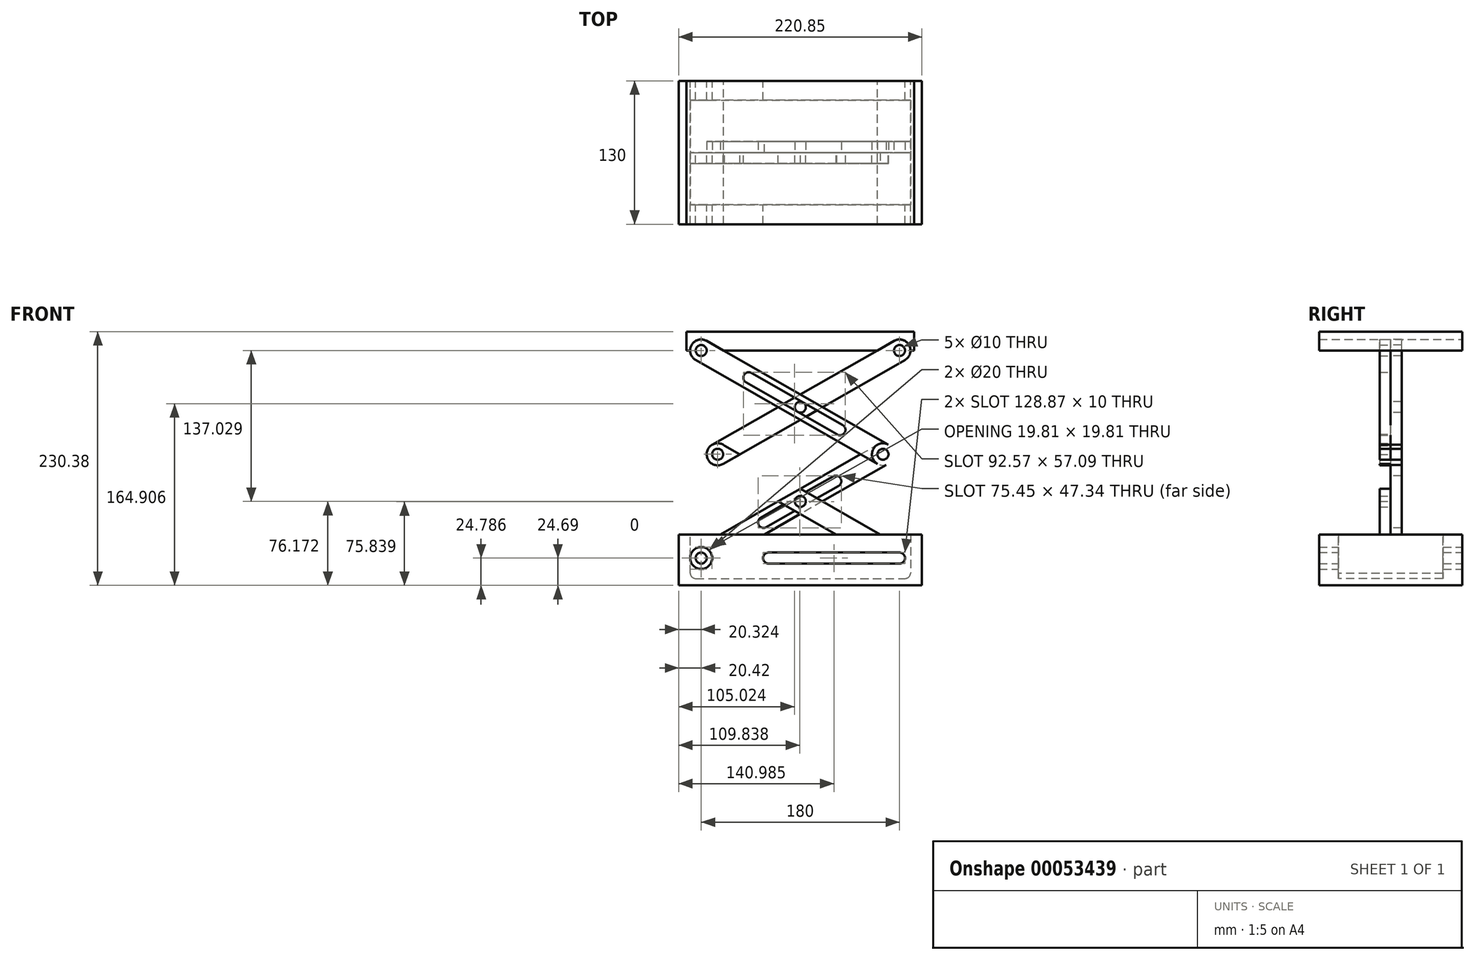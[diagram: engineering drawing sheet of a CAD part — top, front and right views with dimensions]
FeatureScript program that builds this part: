
annotation { "Feature Type Name" : "Feature", "Feature Type Description" : "" }
export const myFeature = defineFeature(function(context is Context, id is Id, definition is map)
    precondition{}
    {
        {
            var Q0;
            Q0=qCreatedBy(makeId("Front.planeOp"),FACE);
            var sketch = newSketch(context, id + "F0", { "sketchPlane" : qUnion([Q0])});
            skLineSegment(sketch, "E0", {"start": v(-81.96, 130.23) * mm, "end": v(83.04, 224.44) * mm, "construction": true});
            skLineSegment(sketch, "E1.bottom", {"start": v(96.47, 241.62) * mm, "end": v(-110.39, 241.62) * mm});
            skLineSegment(sketch, "E1.top", {"start": v(96.47, 224.44) * mm, "end": v(-110.39, 224.44) * mm});
            skLineSegment(sketch, "E1.left", {"start": v(96.47, 241.62) * mm, "end": v(96.47, 224.44) * mm});
            skLineSegment(sketch, "E1.right", {"start": v(-110.39, 241.62) * mm, "end": v(-110.39, 224.44) * mm});
            skCircle(sketch, "E2", {"center": v(83.04, 36.03) * mm, "radius": 5 * mm});
            skCircle(sketch, "E3", {"center": v(-81.96, 130.23) * mm, "radius": 5 * mm});
            skCircle(sketch, "E4", {"center": v(83.04, 224.44) * mm, "radius": 5 * mm});
            skLineSegment(sketch, "E5", {"start": v(-6.96, 224.44) * mm, "end": v(-6.96, -118.03) * mm, "construction": true});
            skCircle(sketch, "E6.MirrorC", {"center": v(-96.96, 224.44) * mm, "radius": 5 * mm});
            skCircle(sketch, "E7.MirrorC", {"center": v(-96.96, 36.03) * mm, "radius": 5 * mm});
            skLineSegment(sketch, "E8.MirrorCS", {"start": v(68.04, 130.23) * mm, "end": v(-96.96, 224.44) * mm, "construction": true});
            skLineSegment(sketch, "E9.MirrorCS", {"start": v(-96.96, 36.03) * mm, "end": v(68.04, 130.23) * mm, "construction": true});
            skCircle(sketch, "E10.MirrorC", {"center": v(68.04, 130.23) * mm, "radius": 5 * mm});
            skLineSegment(sketch, "E11.top", {"start": v(-6.96, 11.24) * mm, "end": v(103.47, 11.24) * mm});
            skLineSegment(sketch, "E11.right", {"start": v(103.47, 57.44) * mm, "end": v(103.47, 11.24) * mm});
            skLineSegment(sketch, "E12", {"start": v(-81.96, 130.23) * mm, "end": v(83.04, 36.03) * mm, "construction": true});
            skCircle(sketch, "E13", {"center": v(83.04, 36.03) * mm, "radius": 10 * mm});
            skCircle(sketch, "E14", {"center": v(-96.96, 36.03) * mm, "radius": 10 * mm});
            skCircle(sketch, "E15", {"center": v(68.04, 130.23) * mm, "radius": 10 * mm});
            skCircle(sketch, "E16", {"center": v(-81.96, 130.23) * mm, "radius": 10 * mm});
            skCircle(sketch, "E17", {"center": v(83.04, 224.44) * mm, "radius": 10 * mm});
            skCircle(sketch, "E18", {"center": v(-96.96, 224.44) * mm, "radius": 10 * mm});
            skLineSegment(sketch, "E19", {"start": v(-102.57, 44.3) * mm, "end": v(63.08, 138.92) * mm});
            skLineSegment(sketch, "E20", {"start": v(74.89, 122.95) * mm, "end": v(-91.99, 27.35) * mm});
            skLineSegment(sketch, "E21", {"start": v(77.54, 27.67) * mm, "end": v(-86.92, 121.55) * mm});
            skLineSegment(sketch, "E22", {"start": v(-75.8, 138.12) * mm, "end": v(88, 44.71) * mm});
            skLineSegment(sketch, "E23", {"start": v(88, 215.76) * mm, "end": v(-77, 121.55) * mm});
            skLineSegment(sketch, "E24", {"start": v(-86.92, 138.92) * mm, "end": v(78.08, 233.12) * mm});
            skLineSegment(sketch, "E25", {"start": v(73, 138.92) * mm, "end": v(-92, 233.12) * mm});
            skLineSegment(sketch, "E26", {"start": v(-101.92, 215.76) * mm, "end": v(63.08, 121.55) * mm});
            skArc(sketch, "E27", {"start": v(27.7, 101.45) * mm, "mid": v(29.57, 108.27) * mm, "end": v(22.75, 110.13) * mm});
            skArc(sketch, "E28", {"start": v(-42.79, 72.71) * mm, "mid": v(-44.65, 65.9) * mm, "end": v(-37.83, 64.03) * mm});
            skLineSegment(sketch, "E29", {"start": v(-42.79, 72.71) * mm, "end": v(22.75, 110.13) * mm});
            skLineSegment(sketch, "E30", {"start": v(27.7, 101.45) * mm, "end": v(-37.83, 64.03) * mm});
            skCircle(sketch, "E31", {"center": v(-6.96, 87.41) * mm, "radius": 5 * mm});
            skArc(sketch, "E32", {"start": v(-51.2, 204.07) * mm, "mid": v(-58.02, 202.2) * mm, "end": v(-56.16, 195.39) * mm});
            skArc(sketch, "E33", {"start": v(26.03, 148.5) * mm, "mid": v(33.19, 149.8) * mm, "end": v(31.48, 156.87) * mm});
            skLineSegment(sketch, "E34", {"start": v(-51.2, 204.07) * mm, "end": v(31.48, 156.87) * mm});
            skLineSegment(sketch, "E35", {"start": v(27.05, 147.92) * mm, "end": v(-56.16, 195.39) * mm});
            skCircle(sketch, "E36", {"center": v(-6.96, 173.05) * mm, "radius": 4.98 * mm});
            skLineSegment(sketch, "E37.MirrorCS", {"start": v(-6.96, 11.24) * mm, "end": v(-117.38, 11.24) * mm});
            skLineSegment(sketch, "E38.MirrorCS", {"start": v(-117.38, 57.44) * mm, "end": v(-117.38, 11.24) * mm});
            skLineSegment(sketch, "E39", {"start": v(-117.38, 57.44) * mm, "end": v(103.47, 57.44) * mm});
            skLineSegment(sketch, "E40", {"start": v(83.04, 36.03) * mm, "end": v(-35.83, 36.03) * mm, "construction": true});
            skCircle(sketch, "E41", {"center": v(-35.83, 36.03) * mm, "radius": 5 * mm});
            skLineSegment(sketch, "E42", {"start": v(83.04, 41.03) * mm, "end": v(-35.83, 41.03) * mm});
            skLineSegment(sketch, "E43", {"start": v(-35.83, 31.03) * mm, "end": v(83.04, 31.03) * mm});
            skSolve(sketch);
        }
        {
            var Q0;
            Q0=makeQuery(id+"F0.imprint","IMPRINT",FACE,{"disambiguationData":[TD([[makeQuery(id+"F0.imprint","IMPRINT",EDGE,{"derivedFrom":sQuery(id+"F0.wireOp",EDGE,"E11.top")}),1.0]])]});
            var Q1;
            {var subQ2=sQuery(id+"F0.wireOp",EDGE,"E42");var subQ7=sQuery(id+"F0.wireOp",EDGE,"E2");var subQ9=makeQuery(id+"F0.imprint","INTERSECT",VERTEX,{"derivedFrom":[subQ7,subQ2]});Q1=makeQuery(id+"F0.imprint","IMPRINT",FACE,{"disambiguationData":[TD([[makeQuery(id+"F0.imprint","IMPRINT",EDGE,{"disambiguationData":[TD([[subQ9,1.0]])],"derivedFrom":subQ7}),-1.0]])]});}
            var Q2;
            {var subQ0=sQuery(id+"F0.wireOp",EDGE,"E22");var subQ1=sQuery(id+"F0.wireOp",EDGE,"E13");var subQ2=makeQuery(id+"F0.imprint","INTERSECT",VERTEX,{"derivedFrom":[subQ1,subQ0]});Q2=makeQuery(id+"F0.imprint","IMPRINT",FACE,{"disambiguationData":[TD([[makeQuery(id+"F0.imprint","IMPRINT",EDGE,{"disambiguationData":[TD([[subQ2,-1.0]])],"derivedFrom":subQ1}),-1.0]])]});}
            var Q3;
            {var subQ0=sQuery(id+"F0.wireOp",EDGE,"E20");var subQ1=sQuery(id+"F0.wireOp",EDGE,"E14");var subQ2=makeQuery(id+"F0.imprint","INTERSECT",VERTEX,{"derivedFrom":[subQ1,subQ0]});Q3=makeQuery(id+"F0.imprint","IMPRINT",FACE,{"disambiguationData":[TD([[makeQuery(id+"F0.imprint","IMPRINT",EDGE,{"disambiguationData":[TD([[subQ2,-1.0]])],"derivedFrom":subQ1}),-1.0]])]});}
            var Q4;
            Q4=makeQuery(id+"F0.imprint","IMPRINT",FACE,{"disambiguationData":[TD([[makeQuery(id+"F0.imprint","IMPRINT",EDGE,{"derivedFrom":sQuery(id+"F0.wireOp",EDGE,"E7.MirrorC")}),1.0]])]});
            var Q5;
            {var subQ0=sQuery(id+"F0.wireOp",EDGE,"E21");var subQ1=sQuery(id+"F0.wireOp",EDGE,"E13");var subQ2=makeQuery(id+"F0.imprint","INTERSECT",VERTEX,{"derivedFrom":[subQ1,subQ0]});Q5=makeQuery(id+"F0.imprint","IMPRINT",FACE,{"disambiguationData":[TD([[makeQuery(id+"F0.imprint","IMPRINT",EDGE,{"disambiguationData":[TD([[subQ2,1.0]])],"derivedFrom":subQ1}),-1.0]])]});}
            extrude(context, id + "F1", {"entities" : qUnion([Q0, Q1, Q2, Q3, Q4, Q5]), "endBound" : BoundingType.SYMMETRIC, "depth" : 130 * mm});
        }
        {
            var Q0;
            Q0=makeQuery(id+"F0.imprint","IMPRINT",FACE,{"disambiguationData":[TD([[makeQuery(id+"F0.imprint","IMPRINT",EDGE,{"derivedFrom":sQuery(id+"F0.wireOp",EDGE,"E1.bottom")}),1.0]])]});
            extrude(context, id + "F2", {"entities" : qUnion([Q0]), "endBound" : BoundingType.SYMMETRIC, "depth" : 130 * mm});
        }
        {
            var Q0;
            {var subQ3=sQuery(id+"F0.wireOp",EDGE,"E25");var subQ5=sQuery(id+"F0.wireOp",EDGE,"E1.top");var subQ6=makeQuery(id+"F0.imprint","INTERSECT",VERTEX,{"derivedFrom":[subQ5,subQ3]});Q0=makeQuery(id+"F0.imprint","IMPRINT",FACE,{"disambiguationData":[TD([[makeQuery(id+"F0.imprint","IMPRINT",EDGE,{"disambiguationData":[TD([[subQ6,-1.0]])],"derivedFrom":subQ5}),1.0]])]});}
            var Q1;
            {var subQ0=sQuery(id+"F0.wireOp",EDGE,"E25");var subQ1=sQuery(id+"F0.wireOp",EDGE,"E1.top");var subQ2=makeQuery(id+"F0.imprint","INTERSECT",VERTEX,{"derivedFrom":[subQ1,subQ0]});Q1=makeQuery(id+"F0.imprint","IMPRINT",FACE,{"disambiguationData":[TD([[makeQuery(id+"F0.imprint","IMPRINT",EDGE,{"disambiguationData":[TD([[subQ2,-1.0]])],"derivedFrom":subQ1}),-1.0]])]});}
            var Q2;
            {var subQ0=sQuery(id+"F0.wireOp",EDGE,"E18");var subQ1=sQuery(id+"F0.wireOp",EDGE,"E1.top");var subQ2=makeQuery(id+"F0.imprint","INTERSECT",VERTEX,{"disambiguationData":[OD(1.0)],"derivedFrom":[subQ1,subQ0]});Q2=makeQuery(id+"F0.imprint","IMPRINT",FACE,{"disambiguationData":[TD([[makeQuery(id+"F0.imprint","IMPRINT",EDGE,{"disambiguationData":[TD([[subQ2,-1.0]])],"derivedFrom":subQ1}),-1.0]])]});}
            var Q3;
            {var subQ1=sQuery(id+"F0.wireOp",EDGE,"E18");var subQ3=sQuery(id+"F0.wireOp",EDGE,"E1.top");var subQ8=makeQuery(id+"F0.imprint","INTERSECT",VERTEX,{"disambiguationData":[OD(1.0)],"derivedFrom":[subQ3,subQ1]});Q3=makeQuery(id+"F0.imprint","IMPRINT",FACE,{"disambiguationData":[TD([[makeQuery(id+"F0.imprint","IMPRINT",EDGE,{"disambiguationData":[TD([[subQ8,-1.0]])],"derivedFrom":subQ3}),1.0]])]});}
            var Q4;
            {var subQ0=sQuery(id+"F0.wireOp",EDGE,"E25");var subQ1=sQuery(id+"F0.wireOp",EDGE,"E23");var subQ2=makeQuery(id+"F0.imprint","INTERSECT",VERTEX,{"derivedFrom":[subQ1,subQ0]});Q4=makeQuery(id+"F0.imprint","IMPRINT",FACE,{"disambiguationData":[TD([[makeQuery(id+"F0.imprint","IMPRINT",EDGE,{"disambiguationData":[TD([[subQ2,-1.0]])],"derivedFrom":subQ1}),-1.0]])]});}
            var Q5;
            {var subQ5=sQuery(id+"F0.wireOp",EDGE,"E19");var subQ6=sQuery(id+"F0.wireOp",EDGE,"E15");var subQ7=makeQuery(id+"F0.imprint","INTERSECT",VERTEX,{"derivedFrom":[subQ6,subQ5]});Q5=makeQuery(id+"F0.imprint","IMPRINT",FACE,{"disambiguationData":[TD([[makeQuery(id+"F0.imprint","IMPRINT",EDGE,{"disambiguationData":[TD([[subQ7,1.0]])],"derivedFrom":subQ6}),-1.0]])]});}
            var Q6;
            {var subQ0=sQuery(id+"F0.wireOp",EDGE,"E19");var subQ1=sQuery(id+"F0.wireOp",EDGE,"E15");var subQ2=makeQuery(id+"F0.imprint","INTERSECT",VERTEX,{"derivedFrom":[subQ1,subQ0]});Q6=makeQuery(id+"F0.imprint","IMPRINT",FACE,{"disambiguationData":[TD([[makeQuery(id+"F0.imprint","IMPRINT",EDGE,{"disambiguationData":[TD([[subQ2,-1.0]])],"derivedFrom":subQ1}),-1.0]])]});}
            var Q7;
            Q7=makeQuery(id+"F0.imprint","IMPRINT",FACE,{"disambiguationData":[TD([[makeQuery(id+"F0.imprint","IMPRINT",EDGE,{"derivedFrom":sQuery(id+"F0.wireOp",EDGE,"E10.MirrorC")}),1.0]])]});
            var Q8;
            {var subQ1=sQuery(id+"F0.wireOp",EDGE,"E16");var subQ9=makeQuery(id+"F0.imprint","IMPRINT",VERTEX,{"derivedFrom":subQ1});Q8=makeQuery(id+"F0.imprint","IMPRINT",FACE,{"disambiguationData":[TD([[makeQuery(id+"F0.imprint","IMPRINT",EDGE,{"disambiguationData":[TD([[subQ9,1.0]])],"derivedFrom":subQ1}),-1.0]])]});}
            var Q9;
            {var subQ0=sQuery(id+"F0.wireOp",EDGE,"E22");var subQ1=sQuery(id+"F0.wireOp",EDGE,"E16");var subQ2=makeQuery(id+"F0.imprint","INTERSECT",VERTEX,{"derivedFrom":[subQ1,subQ0]});Q9=makeQuery(id+"F0.imprint","IMPRINT",FACE,{"disambiguationData":[TD([[makeQuery(id+"F0.imprint","IMPRINT",EDGE,{"disambiguationData":[TD([[subQ2,1.0]])],"derivedFrom":subQ1}),-1.0]])]});}
            var Q10;
            Q10=makeQuery(id+"F0.imprint","IMPRINT",FACE,{"disambiguationData":[TD([[makeQuery(id+"F0.imprint","IMPRINT",EDGE,{"derivedFrom":sQuery(id+"F0.wireOp",EDGE,"E3")}),-1.0]])]});
            var Q11;
            {var subQ0=sQuery(id+"F0.wireOp",EDGE,"E21");var subQ1=sQuery(id+"F0.wireOp",EDGE,"E19");var subQ2=makeQuery(id+"F0.imprint","INTERSECT",VERTEX,{"derivedFrom":[subQ1,subQ0]});Q11=makeQuery(id+"F0.imprint","IMPRINT",FACE,{"disambiguationData":[TD([[makeQuery(id+"F0.imprint","IMPRINT",EDGE,{"disambiguationData":[TD([[subQ2,-1.0]])],"derivedFrom":subQ1}),-1.0]])]});}
            var Q12;
            {var subQ0=sQuery(id+"F0.wireOp",EDGE,"E21");var subQ1=sQuery(id+"F0.wireOp",EDGE,"E11.bottom");var subQ2=makeQuery(id+"F0.imprint","INTERSECT",VERTEX,{"derivedFrom":[subQ1,subQ0]});Q12=makeQuery(id+"F0.imprint","IMPRINT",FACE,{"disambiguationData":[TD([[makeQuery(id+"F0.imprint","IMPRINT",EDGE,{"disambiguationData":[TD([[subQ2,-1.0]])],"derivedFrom":subQ1}),1.0]])]});}
            var Q13;
            {var subQ2=sQuery(id+"F0.wireOp",EDGE,"E11.bottom");var subQ4=sQuery(id+"F0.wireOp",EDGE,"E2");var subQ5=makeQuery(id+"F0.imprint","INTERSECT",VERTEX,{"disambiguationData":[OD(0.0)],"derivedFrom":[subQ4,subQ2]});Q13=makeQuery(id+"F0.imprint","IMPRINT",FACE,{"disambiguationData":[TD([[makeQuery(id+"F0.imprint","IMPRINT",EDGE,{"disambiguationData":[TD([[subQ5,1.0]])],"derivedFrom":subQ4}),-1.0]])]});}
            var Q14;
            {var subQ2=sQuery(id+"F0.wireOp",EDGE,"E11.bottom");var subQ5=sQuery(id+"F0.wireOp",EDGE,"E2");var subQ7=makeQuery(id+"F0.imprint","INTERSECT",VERTEX,{"disambiguationData":[OD(0.0)],"derivedFrom":[subQ5,subQ2]});Q14=makeQuery(id+"F0.imprint","IMPRINT",FACE,{"disambiguationData":[TD([[makeQuery(id+"F0.imprint","IMPRINT",EDGE,{"disambiguationData":[TD([[subQ7,-1.0]])],"derivedFrom":subQ5}),-1.0]])]});}
            var Q15;
            {var subQ0=sQuery(id+"F0.wireOp",EDGE,"E21");var subQ1=sQuery(id+"F0.wireOp",EDGE,"E11.bottom");var subQ2=makeQuery(id+"F0.imprint","INTERSECT",VERTEX,{"derivedFrom":[subQ1,subQ0]});Q15=makeQuery(id+"F0.imprint","IMPRINT",FACE,{"disambiguationData":[TD([[makeQuery(id+"F0.imprint","IMPRINT",EDGE,{"disambiguationData":[TD([[subQ2,-1.0]])],"derivedFrom":subQ1}),-1.0]])]});}
            var Q16;
            {var subQ0=sQuery(id+"F0.wireOp",EDGE,"E29");var subQ1=sQuery(id+"F0.wireOp",EDGE,"E22");var subQ2=makeQuery(id+"F0.imprint","INTERSECT",VERTEX,{"derivedFrom":[subQ1,subQ0]});Q16=makeQuery(id+"F0.imprint","IMPRINT",FACE,{"disambiguationData":[TD([[makeQuery(id+"F0.imprint","IMPRINT",EDGE,{"disambiguationData":[TD([[subQ2,-1.0]])],"derivedFrom":subQ1}),-1.0]])]});}
            var Q17;
            {var subQ0=sQuery(id+"F0.wireOp",EDGE,"E35");var subQ2=sQuery(id+"F0.wireOp",EDGE,"E23");var subQ3=makeQuery(id+"F0.imprint","INTERSECT",VERTEX,{"derivedFrom":[subQ2,subQ0]});Q17=makeQuery(id+"F0.imprint","IMPRINT",FACE,{"disambiguationData":[TD([[makeQuery(id+"F0.imprint","IMPRINT",EDGE,{"disambiguationData":[TD([[subQ3,-1.0]])],"derivedFrom":subQ2}),-1.0]])]});}
            var Q18;
            {var subQ0=sQuery(id+"F0.wireOp",EDGE,"E30");var subQ1=sQuery(id+"F0.wireOp",EDGE,"E21");var subQ2=makeQuery(id+"F0.imprint","INTERSECT",VERTEX,{"derivedFrom":[subQ1,subQ0]});Q18=makeQuery(id+"F0.imprint","IMPRINT",FACE,{"disambiguationData":[TD([[makeQuery(id+"F0.imprint","IMPRINT",EDGE,{"disambiguationData":[TD([[subQ2,-1.0]])],"derivedFrom":subQ1}),-1.0]])]});}
            var Q19;
            {var subQ1=sQuery(id+"F0.wireOp",EDGE,"E22");var subQ4=sQuery(id+"F0.wireOp",EDGE,"E20");var subQ5=makeQuery(id+"F0.imprint","INTERSECT",VERTEX,{"derivedFrom":[subQ4,subQ1]});Q19=makeQuery(id+"F0.imprint","IMPRINT",FACE,{"disambiguationData":[TD([[makeQuery(id+"F0.imprint","IMPRINT",EDGE,{"disambiguationData":[TD([[subQ5,-1.0]])],"derivedFrom":subQ4}),-1.0]])]});}
            var Q20;
            {var subQ0=sQuery(id+"F0.wireOp",EDGE,"E22");var subQ1=sQuery(id+"F0.wireOp",EDGE,"E20");var subQ2=makeQuery(id+"F0.imprint","INTERSECT",VERTEX,{"derivedFrom":[subQ1,subQ0]});Q20=makeQuery(id+"F0.imprint","IMPRINT",FACE,{"disambiguationData":[TD([[makeQuery(id+"F0.imprint","IMPRINT",EDGE,{"disambiguationData":[TD([[subQ2,-1.0]])],"derivedFrom":subQ1}),1.0]])]});}
            var Q21;
            {var subQ0=sQuery(id+"F0.wireOp",EDGE,"E22");var subQ1=sQuery(id+"F0.wireOp",EDGE,"E13");var subQ2=makeQuery(id+"F0.imprint","INTERSECT",VERTEX,{"derivedFrom":[subQ1,subQ0]});Q21=makeQuery(id+"F0.imprint","IMPRINT",FACE,{"disambiguationData":[TD([[makeQuery(id+"F0.imprint","IMPRINT",EDGE,{"disambiguationData":[TD([[subQ2,-1.0]])],"derivedFrom":subQ1}),-1.0]])]});}
            var Q22;
            {var subQ0=sQuery(id+"F0.wireOp",EDGE,"E42");var subQ1=sQuery(id+"F0.wireOp",EDGE,"E13");var subQ2=makeQuery(id+"F0.imprint","INTERSECT",VERTEX,{"derivedFrom":[subQ1,subQ0]});Q22=makeQuery(id+"F0.imprint","IMPRINT",FACE,{"disambiguationData":[TD([[makeQuery(id+"F0.imprint","IMPRINT",EDGE,{"disambiguationData":[TD([[subQ2,-1.0]])],"derivedFrom":subQ1}),-1.0]])]});}
            var Q23;
            {var subQ2=sQuery(id+"F0.wireOp",EDGE,"E42");var subQ7=sQuery(id+"F0.wireOp",EDGE,"E2");var subQ9=makeQuery(id+"F0.imprint","INTERSECT",VERTEX,{"derivedFrom":[subQ7,subQ2]});Q23=makeQuery(id+"F0.imprint","IMPRINT",FACE,{"disambiguationData":[TD([[makeQuery(id+"F0.imprint","IMPRINT",EDGE,{"disambiguationData":[TD([[subQ9,1.0]])],"derivedFrom":subQ7}),-1.0]])]});}
            var Q24;
            {var subQ0=sQuery(id+"F0.wireOp",EDGE,"E21");var subQ1=sQuery(id+"F0.wireOp",EDGE,"E13");var subQ2=makeQuery(id+"F0.imprint","INTERSECT",VERTEX,{"derivedFrom":[subQ1,subQ0]});Q24=makeQuery(id+"F0.imprint","IMPRINT",FACE,{"disambiguationData":[TD([[makeQuery(id+"F0.imprint","IMPRINT",EDGE,{"disambiguationData":[TD([[subQ2,1.0]])],"derivedFrom":subQ1}),-1.0]])]});}
            extrude(context, id + "F3", {"entities" : qUnion([Q0, Q1, Q2, Q3, Q4, Q5, Q6, Q7, Q8, Q9, Q10, Q11, Q12, Q13, Q14, Q15, Q16, Q17, Q18, Q19, Q20, Q21, Q22, Q23, Q24]), "depth" : 10 * mm});
        }
        {
            var Q0;
            {var subQ1=sQuery(id+"F0.wireOp",EDGE,"E17");var subQ5=sQuery(id+"F0.wireOp",EDGE,"E1.top");var subQ6=makeQuery(id+"F0.imprint","INTERSECT",VERTEX,{"disambiguationData":[OD(1.0)],"derivedFrom":[subQ5,subQ1]});Q0=makeQuery(id+"F0.imprint","IMPRINT",FACE,{"disambiguationData":[TD([[makeQuery(id+"F0.imprint","IMPRINT",EDGE,{"disambiguationData":[TD([[subQ6,-1.0]])],"derivedFrom":subQ5}),1.0]])]});}
            var Q1;
            {var subQ1=sQuery(id+"F0.wireOp",EDGE,"E17");var subQ3=sQuery(id+"F0.wireOp",EDGE,"E1.top");var subQ9=makeQuery(id+"F0.imprint","INTERSECT",VERTEX,{"disambiguationData":[OD(0.0)],"derivedFrom":[subQ3,subQ1]});Q1=makeQuery(id+"F0.imprint","IMPRINT",FACE,{"disambiguationData":[TD([[makeQuery(id+"F0.imprint","IMPRINT",EDGE,{"disambiguationData":[TD([[subQ9,-1.0]])],"derivedFrom":subQ3}),1.0]])]});}
            var Q2;
            {var subQ0=sQuery(id+"F0.wireOp",EDGE,"E17");var subQ2=sQuery(id+"F0.wireOp",EDGE,"E1.top");var subQ3=makeQuery(id+"F0.imprint","INTERSECT",VERTEX,{"disambiguationData":[OD(0.0)],"derivedFrom":[subQ2,subQ0]});Q2=makeQuery(id+"F0.imprint","IMPRINT",FACE,{"disambiguationData":[TD([[makeQuery(id+"F0.imprint","IMPRINT",EDGE,{"disambiguationData":[TD([[subQ3,-1.0]])],"derivedFrom":subQ2}),-1.0]])]});}
            var Q3;
            {var subQ0=sQuery(id+"F0.wireOp",EDGE,"E17");var subQ1=sQuery(id+"F0.wireOp",EDGE,"E1.top");var subQ2=makeQuery(id+"F0.imprint","INTERSECT",VERTEX,{"disambiguationData":[OD(1.0)],"derivedFrom":[subQ1,subQ0]});Q3=makeQuery(id+"F0.imprint","IMPRINT",FACE,{"disambiguationData":[TD([[makeQuery(id+"F0.imprint","IMPRINT",EDGE,{"disambiguationData":[TD([[subQ2,-1.0]])],"derivedFrom":subQ1}),-1.0]])]});}
            var Q4;
            {var subQ0=sQuery(id+"F0.wireOp",EDGE,"E25");var subQ1=sQuery(id+"F0.wireOp",EDGE,"E23");var subQ2=makeQuery(id+"F0.imprint","INTERSECT",VERTEX,{"derivedFrom":[subQ1,subQ0]});Q4=makeQuery(id+"F0.imprint","IMPRINT",FACE,{"disambiguationData":[TD([[makeQuery(id+"F0.imprint","IMPRINT",EDGE,{"disambiguationData":[TD([[subQ2,-1.0]])],"derivedFrom":subQ1}),-1.0]])]});}
            var Q5;
            {var subQ1=sQuery(id+"F0.wireOp",EDGE,"E16");var subQ6=sQuery(id+"F0.wireOp",EDGE,"E22");var subQ9=makeQuery(id+"F0.imprint","INTERSECT",VERTEX,{"derivedFrom":[subQ1,subQ6]});Q5=makeQuery(id+"F0.imprint","IMPRINT",FACE,{"disambiguationData":[TD([[makeQuery(id+"F0.imprint","IMPRINT",EDGE,{"disambiguationData":[TD([[subQ9,-1.0]])],"derivedFrom":subQ1}),-1.0]])]});}
            var Q6;
            {var subQ0=sQuery(id+"F0.wireOp",EDGE,"E22");var subQ1=sQuery(id+"F0.wireOp",EDGE,"E16");var subQ2=makeQuery(id+"F0.imprint","INTERSECT",VERTEX,{"derivedFrom":[subQ1,subQ0]});Q6=makeQuery(id+"F0.imprint","IMPRINT",FACE,{"disambiguationData":[TD([[makeQuery(id+"F0.imprint","IMPRINT",EDGE,{"disambiguationData":[TD([[subQ2,1.0]])],"derivedFrom":subQ1}),-1.0]])]});}
            var Q7;
            Q7=makeQuery(id+"F0.imprint","IMPRINT",FACE,{"disambiguationData":[TD([[makeQuery(id+"F0.imprint","IMPRINT",EDGE,{"derivedFrom":sQuery(id+"F0.wireOp",EDGE,"E3")}),-1.0]])]});
            var Q8;
            {var subQ5=sQuery(id+"F0.wireOp",EDGE,"E15");var subQ7=sQuery(id+"F0.wireOp",EDGE,"E26");var subQ9=makeQuery(id+"F0.imprint","INTERSECT",VERTEX,{"derivedFrom":[subQ5,subQ7]});Q8=makeQuery(id+"F0.imprint","IMPRINT",FACE,{"disambiguationData":[TD([[makeQuery(id+"F0.imprint","IMPRINT",EDGE,{"disambiguationData":[TD([[subQ9,-1.0]])],"derivedFrom":subQ5}),-1.0]])]});}
            var Q9;
            Q9=makeQuery(id+"F0.imprint","IMPRINT",FACE,{"disambiguationData":[TD([[makeQuery(id+"F0.imprint","IMPRINT",EDGE,{"derivedFrom":sQuery(id+"F0.wireOp",EDGE,"E10.MirrorC")}),1.0]])]});
            var Q10;
            {var subQ0=sQuery(id+"F0.wireOp",EDGE,"E19");var subQ1=sQuery(id+"F0.wireOp",EDGE,"E15");var subQ2=makeQuery(id+"F0.imprint","INTERSECT",VERTEX,{"derivedFrom":[subQ1,subQ0]});Q10=makeQuery(id+"F0.imprint","IMPRINT",FACE,{"disambiguationData":[TD([[makeQuery(id+"F0.imprint","IMPRINT",EDGE,{"disambiguationData":[TD([[subQ2,-1.0]])],"derivedFrom":subQ1}),-1.0]])]});}
            var Q11;
            {var subQ0=sQuery(id+"F0.wireOp",EDGE,"E21");var subQ1=sQuery(id+"F0.wireOp",EDGE,"E19");var subQ2=makeQuery(id+"F0.imprint","INTERSECT",VERTEX,{"derivedFrom":[subQ1,subQ0]});Q11=makeQuery(id+"F0.imprint","IMPRINT",FACE,{"disambiguationData":[TD([[makeQuery(id+"F0.imprint","IMPRINT",EDGE,{"disambiguationData":[TD([[subQ2,-1.0]])],"derivedFrom":subQ1}),-1.0]])]});}
            var Q12;
            {var subQ1=sQuery(id+"F0.wireOp",EDGE,"E11.bottom");var subQ6=sQuery(id+"F0.wireOp",EDGE,"E14");var subQ9=makeQuery(id+"F0.imprint","INTERSECT",VERTEX,{"disambiguationData":[OD(1.0)],"derivedFrom":[subQ1,subQ6]});Q12=makeQuery(id+"F0.imprint","IMPRINT",FACE,{"disambiguationData":[TD([[makeQuery(id+"F0.imprint","IMPRINT",EDGE,{"disambiguationData":[TD([[subQ9,-1.0]])],"derivedFrom":subQ1}),1.0]])]});}
            var Q13;
            {var subQ3=sQuery(id+"F0.wireOp",EDGE,"E11.bottom");var subQ5=sQuery(id+"F0.wireOp",EDGE,"E7.MirrorC");var subQ8=makeQuery(id+"F0.imprint","INTERSECT",VERTEX,{"disambiguationData":[OD(0.0)],"derivedFrom":[subQ5,subQ3]});Q13=makeQuery(id+"F0.imprint","IMPRINT",FACE,{"disambiguationData":[TD([[makeQuery(id+"F0.imprint","IMPRINT",EDGE,{"disambiguationData":[TD([[subQ8,-1.0]])],"derivedFrom":subQ5}),1.0]])]});}
            var Q14;
            {var subQ2=sQuery(id+"F0.wireOp",EDGE,"E11.bottom");var subQ4=sQuery(id+"F0.wireOp",EDGE,"E7.MirrorC");var subQ5=makeQuery(id+"F0.imprint","INTERSECT",VERTEX,{"disambiguationData":[OD(0.0)],"derivedFrom":[subQ4,subQ2]});Q14=makeQuery(id+"F0.imprint","IMPRINT",FACE,{"disambiguationData":[TD([[makeQuery(id+"F0.imprint","IMPRINT",EDGE,{"disambiguationData":[TD([[subQ5,1.0]])],"derivedFrom":subQ4}),1.0]])]});}
            var Q15;
            {var subQ0=sQuery(id+"F0.wireOp",EDGE,"E14");var subQ1=sQuery(id+"F0.wireOp",EDGE,"E11.bottom");var subQ2=makeQuery(id+"F0.imprint","INTERSECT",VERTEX,{"disambiguationData":[OD(1.0)],"derivedFrom":[subQ1,subQ0]});Q15=makeQuery(id+"F0.imprint","IMPRINT",FACE,{"disambiguationData":[TD([[makeQuery(id+"F0.imprint","IMPRINT",EDGE,{"disambiguationData":[TD([[subQ2,-1.0]])],"derivedFrom":subQ1}),-1.0]])]});}
            var Q16;
            {var subQ0=sQuery(id+"F0.wireOp",EDGE,"E22");var subQ1=sQuery(id+"F0.wireOp",EDGE,"E20");var subQ2=makeQuery(id+"F0.imprint","INTERSECT",VERTEX,{"derivedFrom":[subQ1,subQ0]});Q16=makeQuery(id+"F0.imprint","IMPRINT",FACE,{"disambiguationData":[TD([[makeQuery(id+"F0.imprint","IMPRINT",EDGE,{"disambiguationData":[TD([[subQ2,-1.0]])],"derivedFrom":subQ1}),-1.0]])]});}
            var Q17;
            {var subQ0=sQuery(id+"F0.wireOp",EDGE,"E35");var subQ2=sQuery(id+"F0.wireOp",EDGE,"E23");var subQ3=makeQuery(id+"F0.imprint","INTERSECT",VERTEX,{"derivedFrom":[subQ2,subQ0]});Q17=makeQuery(id+"F0.imprint","IMPRINT",FACE,{"disambiguationData":[TD([[makeQuery(id+"F0.imprint","IMPRINT",EDGE,{"disambiguationData":[TD([[subQ3,-1.0]])],"derivedFrom":subQ2}),-1.0]])]});}
            var Q18;
            {var subQ0=sQuery(id+"F0.wireOp",EDGE,"E36");Q18=makeQuery(id+"F0.imprint","IMPRINT",FACE,{"disambiguationData":[TD([[makeQuery(id+"F0.imprint","IMPRINT",EDGE,{"derivedFrom":subQ0}),-1.0]])]});}
            var Q19;
            {var subQ11=sQuery(id+"F0.wireOp",EDGE,"E28");Q19=makeQuery(id+"F0.imprint","IMPRINT",FACE,{"disambiguationData":[TD([[makeQuery(id+"F0.imprint","IMPRINT",EDGE,{"derivedFrom":subQ11}),-1.0]])]});}
            var Q20;
            {var subQ0=sQuery(id+"F0.wireOp",EDGE,"E20");var subQ1=sQuery(id+"F0.wireOp",EDGE,"E14");var subQ2=makeQuery(id+"F0.imprint","INTERSECT",VERTEX,{"derivedFrom":[subQ1,subQ0]});Q20=makeQuery(id+"F0.imprint","IMPRINT",FACE,{"disambiguationData":[TD([[makeQuery(id+"F0.imprint","IMPRINT",EDGE,{"disambiguationData":[TD([[subQ2,-1.0]])],"derivedFrom":subQ1}),-1.0]])]});}
            var Q21;
            Q21=makeQuery(id+"F0.imprint","IMPRINT",FACE,{"disambiguationData":[TD([[makeQuery(id+"F0.imprint","IMPRINT",EDGE,{"derivedFrom":sQuery(id+"F0.wireOp",EDGE,"E7.MirrorC")}),1.0]])]});
            extrude(context, id + "F4", {"entities" : qUnion([Q0, Q1, Q2, Q3, Q4, Q5, Q6, Q7, Q8, Q9, Q10, Q11, Q12, Q13, Q14, Q15, Q16, Q17, Q18, Q19, Q20, Q21]), "oppositeDirection" : true, "depth" : 10 * mm});
        }
        {
            var Q0;
            Q0=qCreatedBy(makeId("Front.planeOp"),FACE);
            var sketch = newSketch(context, id + "F5", { "sketchPlane" : qUnion([Q0])});
            skLineSegment(sketch, "E44.top", {"start": v(-101.96, 17.44) * mm, "end": v(88.04, 17.44) * mm});
            skPoint(sketch, "E45.visualSharp", {"position": v(-106.96, 17.44) * mm});
            skArc(sketch, "E45.filletArc", {"start": v(-106.96, 22.24) * mm, "mid": v(-105.43, 18.84) * mm, "end": v(-101.96, 17.44) * mm});
            skLineSegment(sketch, "E46.0.0", {"start": v(93.04, 57.44) * mm, "end": v(-106.96, 57.44) * mm});
            skLineSegment(sketch, "E47", {"start": v(-6.96, 57.44) * mm, "end": v(-6.96, 11.24) * mm, "construction": true});
            skLineSegment(sketch, "E48.MirrorCS", {"start": v(93.04, 57.44) * mm, "end": v(93.04, 22.44) * mm});
            skPoint(sketch, "E49.orphan", {"position": v(93.04, 22.24) * mm});
            skPoint(sketch, "E50.visualSharp", {"position": v(93.04, 17.44) * mm});
            skArc(sketch, "E50.filletArc", {"start": v(88.04, 17.44) * mm, "mid": v(91.58, 18.9) * mm, "end": v(93.04, 22.44) * mm});
            skLineSegment(sketch, "E51", {"start": v(-106.96, 22.24) * mm, "end": v(-106.96, 57.44) * mm});
            skSolve(sketch);
        }
        {
            var Q0;
            Q0=makeQuery(id+"F5.imprint","IMPRINT",FACE,{"disambiguationData":[TD([[makeQuery(id+"F5.imprint","IMPRINT",EDGE,{"derivedFrom":sQuery(id+"F5.wireOp",EDGE,"E44.top")}),1.0]])]});
            extrude(context, id + "F6", {"entities" : qUnion([Q0]), "operationType" : NewBodyOperationType.REMOVE, "endBound" : BoundingType.SYMMETRIC, "oppositeDirection" : true, "depth" : 95 * mm});
        }
    });
